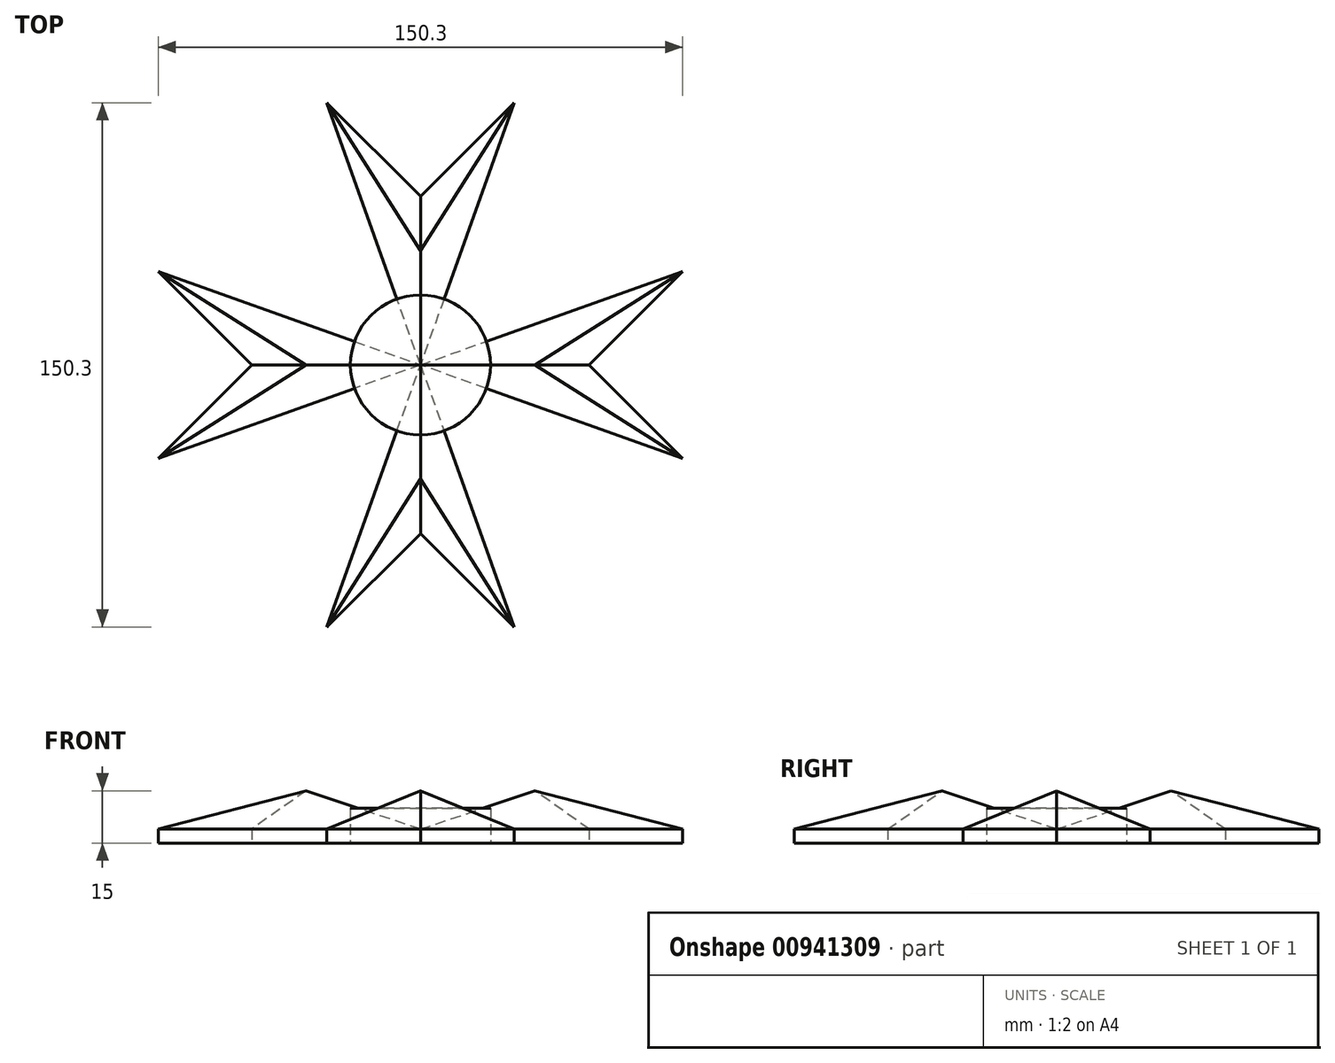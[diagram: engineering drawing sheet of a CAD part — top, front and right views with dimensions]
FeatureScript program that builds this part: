
annotation { "Feature Type Name" : "Feature", "Feature Type Description" : "" }
export const myFeature = defineFeature(function(context is Context, id is Id, definition is map)
    precondition{}
    {
        {
            var Q0;
            Q0=qCreatedBy(makeId("Top.planeOp"),FACE);
            var sketch = newSketch(context, id + "F0", { "sketchPlane" : qUnion([Q0])});
            skLineSegment(sketch, "E0", {"start": v(0, 0) * mm, "end": v(-75.15, 26.8) * mm});
            skLineSegment(sketch, "E1", {"start": v(-75.15, 26.8) * mm, "end": v(-48.36, 0) * mm});
            skLineSegment(sketch, "E2", {"start": v(-48.36, 0) * mm, "end": v(-75.15, -26.8) * mm});
            skLineSegment(sketch, "E3", {"start": v(-75.15, -26.8) * mm, "end": v(0, 0) * mm});
            skPoint(sketch, "E4.start.orphan", {"position": v(-75.15, 0) * mm});
            skLineSegment(sketch, "E5.1.0", {"start": v(-26.8, 75.15) * mm, "end": v(0, 0) * mm});
            skLineSegment(sketch, "E5.1.1", {"start": v(0, 48.36) * mm, "end": v(-26.8, 75.15) * mm});
            skLineSegment(sketch, "E5.1.2", {"start": v(26.8, 75.15) * mm, "end": v(0, 48.36) * mm});
            skLineSegment(sketch, "E5.1.3", {"start": v(0, 0) * mm, "end": v(26.8, 75.15) * mm});
            skLineSegment(sketch, "E5.2.0", {"start": v(75.15, 26.8) * mm, "end": v(0, 0) * mm});
            skLineSegment(sketch, "E5.2.1", {"start": v(48.36, 0) * mm, "end": v(75.15, 26.8) * mm});
            skLineSegment(sketch, "E5.2.2", {"start": v(75.15, -26.8) * mm, "end": v(48.36, 0) * mm});
            skLineSegment(sketch, "E5.2.3", {"start": v(0, 0) * mm, "end": v(75.15, -26.8) * mm});
            skLineSegment(sketch, "E5.3.0", {"start": v(26.8, -75.15) * mm, "end": v(0, 0) * mm});
            skLineSegment(sketch, "E5.3.1", {"start": v(0, -48.36) * mm, "end": v(26.8, -75.15) * mm});
            skLineSegment(sketch, "E5.3.2", {"start": v(-26.8, -75.15) * mm, "end": v(0, -48.36) * mm});
            skLineSegment(sketch, "E5.3.3", {"start": v(0, 0) * mm, "end": v(-26.8, -75.15) * mm});
            skPoint(sketch, "E5.center", {"position": v(0, 0) * mm});
            skLineSegment(sketch, "E5.anchor1", {"start": v(0, 0) * mm, "end": v(-75.15, -26.8) * mm, "construction": true});
            skLineSegment(sketch, "E5.anchor2", {"start": v(0, 0) * mm, "end": v(26.8, -75.15) * mm, "construction": true});
            skSolve(sketch);
        }
        {
            var Q0;
            Q0=makeQuery(id+"F0.imprint","IMPRINT",FACE,{"disambiguationData":[TD([[makeQuery(id+"F0.imprint","IMPRINT",EDGE,{"derivedFrom":sQuery(id+"F0.wireOp",EDGE,"E5.2.0")}),1.0]])]});
            var Q1;
            Q1=makeQuery(id+"F0.imprint","IMPRINT",FACE,{"disambiguationData":[TD([[makeQuery(id+"F0.imprint","IMPRINT",EDGE,{"derivedFrom":sQuery(id+"F0.wireOp",EDGE,"E5.1.0")}),1.0]])]});
            var Q2;
            Q2=makeQuery(id+"F0.imprint","IMPRINT",FACE,{"disambiguationData":[TD([[makeQuery(id+"F0.imprint","IMPRINT",EDGE,{"derivedFrom":sQuery(id+"F0.wireOp",EDGE,"E0")}),1.0]])]});
            var Q3;
            Q3=makeQuery(id+"F0.imprint","IMPRINT",FACE,{"disambiguationData":[TD([[makeQuery(id+"F0.imprint","IMPRINT",EDGE,{"derivedFrom":sQuery(id+"F0.wireOp",EDGE,"E5.3.0")}),1.0]])]});
            extrude(context, id + "F1", {"entities" : qUnion([Q0, Q1, Q2, Q3]), "depth" : 15 * mm, "offsetDistance" : 25 * mm});
        }
        {
            var Q0;
            Q0=makeQuery(id+"F1.opExtrude","CAP_FACE",FACE,{"disambiguationData":[OSD([sQuery(id+"F0.wireOp",EDGE,"E5.3.0"),sQuery(id+"F0.wireOp",EDGE,"E5.3.1"),sQuery(id+"F0.wireOp",EDGE,"E5.3.2"),sQuery(id+"F0.wireOp",EDGE,"E5.3.3")])],"isStart":false});
            var Q1;
            Q1=makeQuery(id+"F1.opExtrude","CAP_FACE",FACE,{"disambiguationData":[OSD([sQuery(id+"F0.wireOp",EDGE,"E5.2.0"),sQuery(id+"F0.wireOp",EDGE,"E5.2.1"),sQuery(id+"F0.wireOp",EDGE,"E5.2.2"),sQuery(id+"F0.wireOp",EDGE,"E5.2.3")])],"isStart":false});
            var Q2;
            Q2=makeQuery(id+"F1.opExtrude","CAP_FACE",FACE,{"disambiguationData":[OSD([sQuery(id+"F0.wireOp",EDGE,"E5.1.0"),sQuery(id+"F0.wireOp",EDGE,"E5.1.1"),sQuery(id+"F0.wireOp",EDGE,"E5.1.2"),sQuery(id+"F0.wireOp",EDGE,"E5.1.3")])],"isStart":false});
            var Q3;
            Q3=makeQuery(id+"F1.opExtrude","CAP_FACE",FACE,{"disambiguationData":[OSD([sQuery(id+"F0.wireOp",EDGE,"E0"),sQuery(id+"F0.wireOp",EDGE,"E1"),sQuery(id+"F0.wireOp",EDGE,"E2"),sQuery(id+"F0.wireOp",EDGE,"E3")])],"isStart":false});
            chamfer(context, id + "F2", {"entities" : qUnion([Q0, Q1, Q2, Q3]), "width" : 11 * mm, "tangentPropagation" : true});
        }
        {
            var Q0;
            Q0=qCreatedBy(makeId("Top.planeOp"),FACE);
            var sketch = newSketch(context, id + "F3", { "sketchPlane" : qUnion([Q0])});
            skCircle(sketch, "E6", {"center": v(0, 0) * mm, "radius": 20.07 * mm});
            skSolve(sketch);
        }
        {
            var Q0;
            Q0=makeQuery(id+"F3.imprint","IMPRINT",FACE,{"disambiguationData":[TD([[makeQuery(id+"F3.imprint","IMPRINT",EDGE,{"derivedFrom":sQuery(id+"F3.wireOp",EDGE,"E6")}),1.0]])]});
            extrude(context, id + "F4", {"entities" : qUnion([Q0]), "depth" : 10 * mm, "offsetDistance" : 25 * mm});
        }
    });
